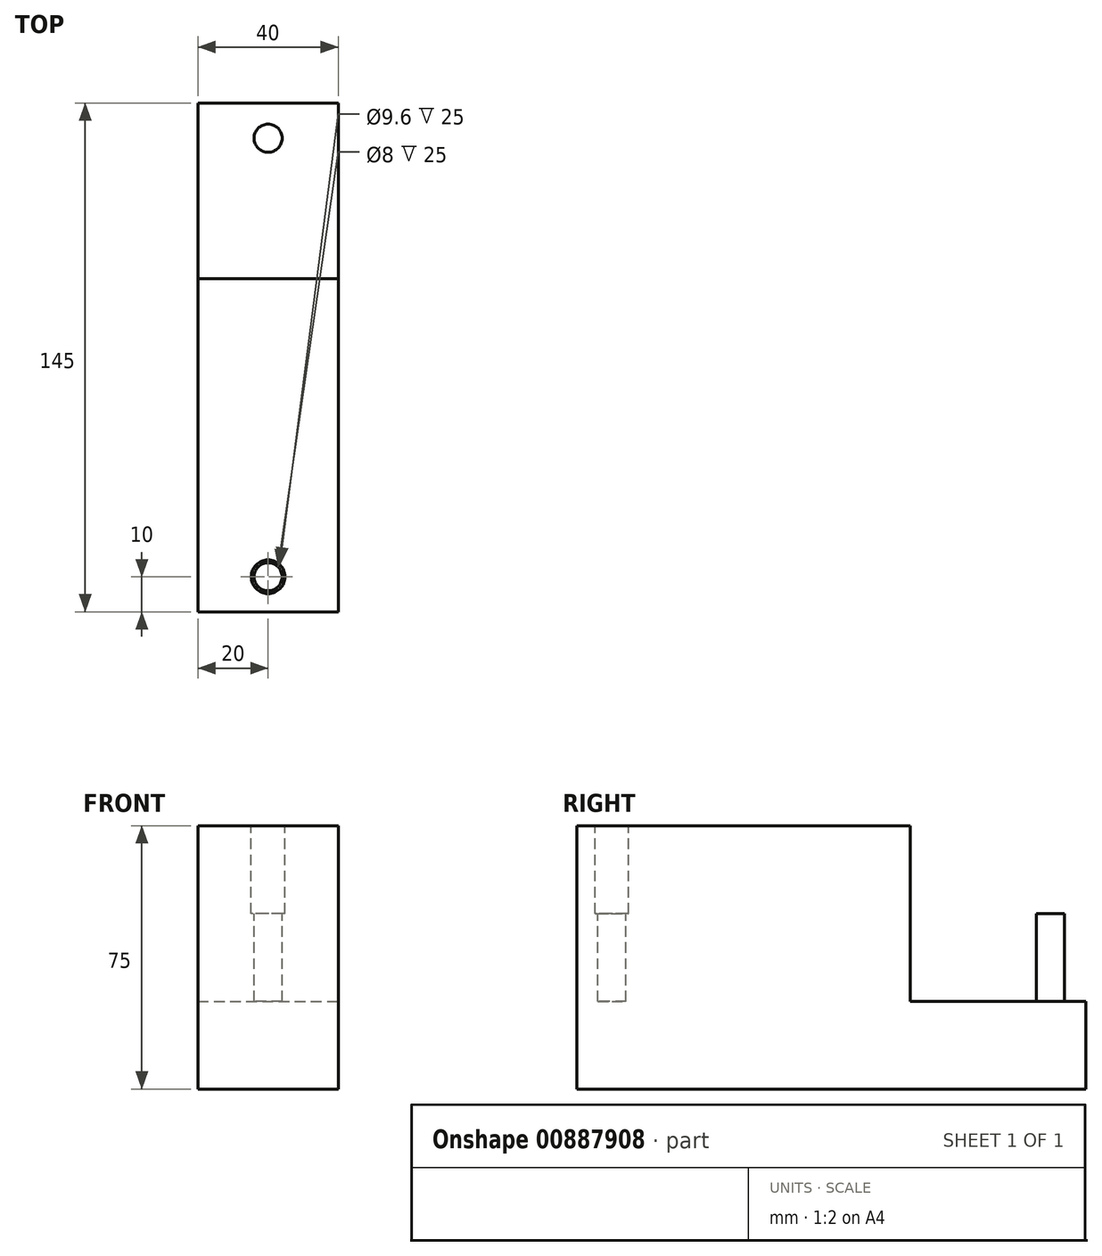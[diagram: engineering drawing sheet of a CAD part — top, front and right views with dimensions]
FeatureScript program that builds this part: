
annotation { "Feature Type Name" : "Feature", "Feature Type Description" : "" }
export const myFeature = defineFeature(function(context is Context, id is Id, definition is map)
    precondition{}
    {
        {
            var Q0;
            Q0=qCreatedBy(makeId("Top.planeOp"),FACE);
            var sketch = newSketch(context, id + "F0", { "sketchPlane" : qUnion([Q0])});
            skLineSegment(sketch, "E0.bottom", {"start": v(-20, 72.5) * mm, "end": v(20, 72.5) * mm});
            skLineSegment(sketch, "E0.top", {"start": v(-20, -72.5) * mm, "end": v(20, -72.5) * mm});
            skLineSegment(sketch, "E0.left", {"start": v(-20, 72.5) * mm, "end": v(-20, -72.5) * mm});
            skLineSegment(sketch, "E0.right", {"start": v(20, 72.5) * mm, "end": v(20, -72.5) * mm});
            skPoint(sketch, "E0.middle", {"position": v(0, 0) * mm});
            skSolve(sketch);
        }
        {
            var Q0;
            Q0=makeQuery(id+"F0.imprint","IMPRINT",FACE,{"disambiguationData":[TD([[makeQuery(id+"F0.imprint","IMPRINT",EDGE,{"derivedFrom":sQuery(id+"F0.wireOp",EDGE,"E0.bottom")}),-1.0]])]});
            extrude(context, id + "F1", {"entities" : qUnion([Q0]), "depth" : 75 * mm, "offsetDistance" : 25 * mm});
        }
        {
            var Q0;
            Q0=makeQuery(id+"F1.opExtrude","CAP_FACE",FACE,{"disambiguationData":[OSD([sQuery(id+"F0.wireOp",EDGE,"E0.bottom"),sQuery(id+"F0.wireOp",EDGE,"E0.top"),sQuery(id+"F0.wireOp",EDGE,"E0.left"),sQuery(id+"F0.wireOp",EDGE,"E0.right")])],"isStart":false});
            var sketch = newSketch(context, id + "F2", { "sketchPlane" : qUnion([Q0])});
            skCircle(sketch, "E1", {"center": v(0, 62.5) * mm, "radius": 4 * mm});
            skCircle(sketch, "E2.MirrorC", {"center": v(0, -62.5) * mm, "radius": 4 * mm});
            skLineSegment(sketch, "E3.bottom", {"start": v(-20, 72.5) * mm, "end": v(20, 72.5) * mm});
            skLineSegment(sketch, "E3.top", {"start": v(-20, 22.5) * mm, "end": v(20, 22.5) * mm});
            skLineSegment(sketch, "E3.left", {"start": v(-20, 72.5) * mm, "end": v(-20, 22.5) * mm});
            skLineSegment(sketch, "E3.right", {"start": v(20, 72.5) * mm, "end": v(20, 22.5) * mm});
            skLineSegment(sketch, "E4.MirrorCS", {"start": v(-20, -72.5) * mm, "end": v(20, -72.5) * mm});
            skLineSegment(sketch, "E5.MirrorCS", {"start": v(20, -72.5) * mm, "end": v(20, -22.5) * mm});
            skLineSegment(sketch, "E6.MirrorCS", {"start": v(-20, -22.5) * mm, "end": v(20, -22.5) * mm});
            skLineSegment(sketch, "E7.MirrorCS", {"start": v(-20, -72.5) * mm, "end": v(-20, -22.5) * mm});
            skSolve(sketch);
        }
        {
            var Q0;
            Q0=makeQuery(id+"F2.imprint","IMPRINT",FACE,{"disambiguationData":[TD([[makeQuery(id+"F2.imprint","IMPRINT",EDGE,{"derivedFrom":sQuery(id+"F2.wireOp",EDGE,"E2.MirrorC")}),1.0]])]});
            var Q1;
            Q1=makeQuery(id+"F2.imprint","IMPRINT",FACE,{"disambiguationData":[TD([[makeQuery(id+"F2.imprint","IMPRINT",EDGE,{"derivedFrom":sQuery(id+"F2.wireOp",EDGE,"E1")}),-1.0]])]});
            extrude(context, id + "F3", {"entities" : qUnion([Q0, Q1]), "operationType" : NewBodyOperationType.REMOVE, "oppositeDirection" : true, "depth" : (75 - 25) * mm, "offsetDistance" : 25 * mm});
        }
        {
            var Q0;
            {var subQ0=sQuery(id+"F0.wireOp",EDGE,"E0.left");var subQ1=sQuery(id+"F0.wireOp",EDGE,"E0.right");Q0=makeQuery(id+"F3.boolean.opBoolean","SPLIT",FACE,{"disambiguationData":[TD([makeQuery(id+"F1.opExtrude","SWEPT_FACE",FACE,{"disambiguationData":[OSD([subQ0])]})])],"derivedFrom":makeQuery(id+"F1.opExtrude","CAP_FACE",FACE,{"disambiguationData":[OSD([sQuery(id+"F0.wireOp",EDGE,"E0.bottom"),sQuery(id+"F0.wireOp",EDGE,"E0.top"),subQ0,subQ1])],"isStart":false})});}
            var sketch = newSketch(context, id + "F4", { "sketchPlane" : qUnion([Q0])});
            skCircle(sketch, "E8", {"center": v(0, 62.5) * mm, "radius": 4.54 * mm});
            skPoint(sketch, "E8.centerSnap0", {"position": v(0, 52.5) * mm});
            skCircle(sketch, "E9", {"center": v(0, -62.5) * mm, "radius": 4.8 * mm});
            skSolve(sketch);
        }
        {
            var Q0;
            Q0 = qSketchRegion(id + "F4", true);
            extrude(context, id + "F5", {"entities" : qUnion([Q0]), "operationType" : NewBodyOperationType.REMOVE, "oppositeDirection" : true, "depth" : (75 - 50) * mm, "offsetDistance" : 25 * mm});
        }
    });
